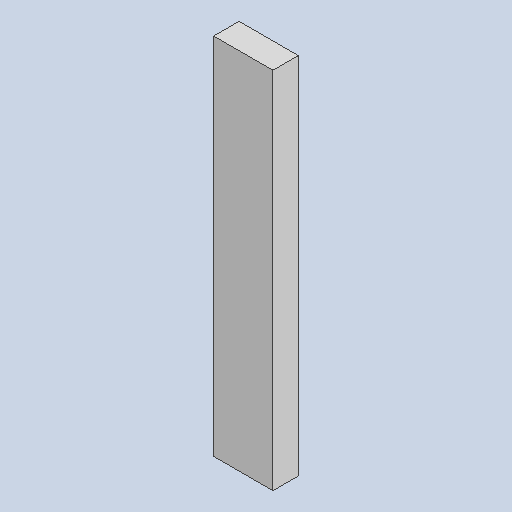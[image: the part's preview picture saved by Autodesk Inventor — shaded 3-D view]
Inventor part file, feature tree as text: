
AUTODESK INVENTOR PART (.ipt)
format: ipt  version: 2025 (Build 290162000, 162)  size: 137,216 bytes
history: native  units: in
note: dims shown in document units (in); Inventor stores cm internally (conversion verified against a paired STEP export)
features: other x4, reference x3, extrude x1, sketch x1
ambient origin geometry x8: Origin, YZ Plane, XZ Plane, XY Plane, X Axis, Y Axis, Z Axis, Center Point
bodies: Solid1 (feature_tree)
feature tree (9):
  extrude  "Extrusion1"  Depth=3.5in
  sketch  "Sketch1"  dims[d1=1.5in d2=0.0in d3=3.5in]
  reference  "Reference1"
  reference  "Reference2"
  reference  "Reference3"
  other  "<userpath>\Documents\Tburn24\F_Legs2\F_Legs2.iam"
  other  "F_Legs2.iam"
  other  "side-side1:1"
  other  "side-side:2"
